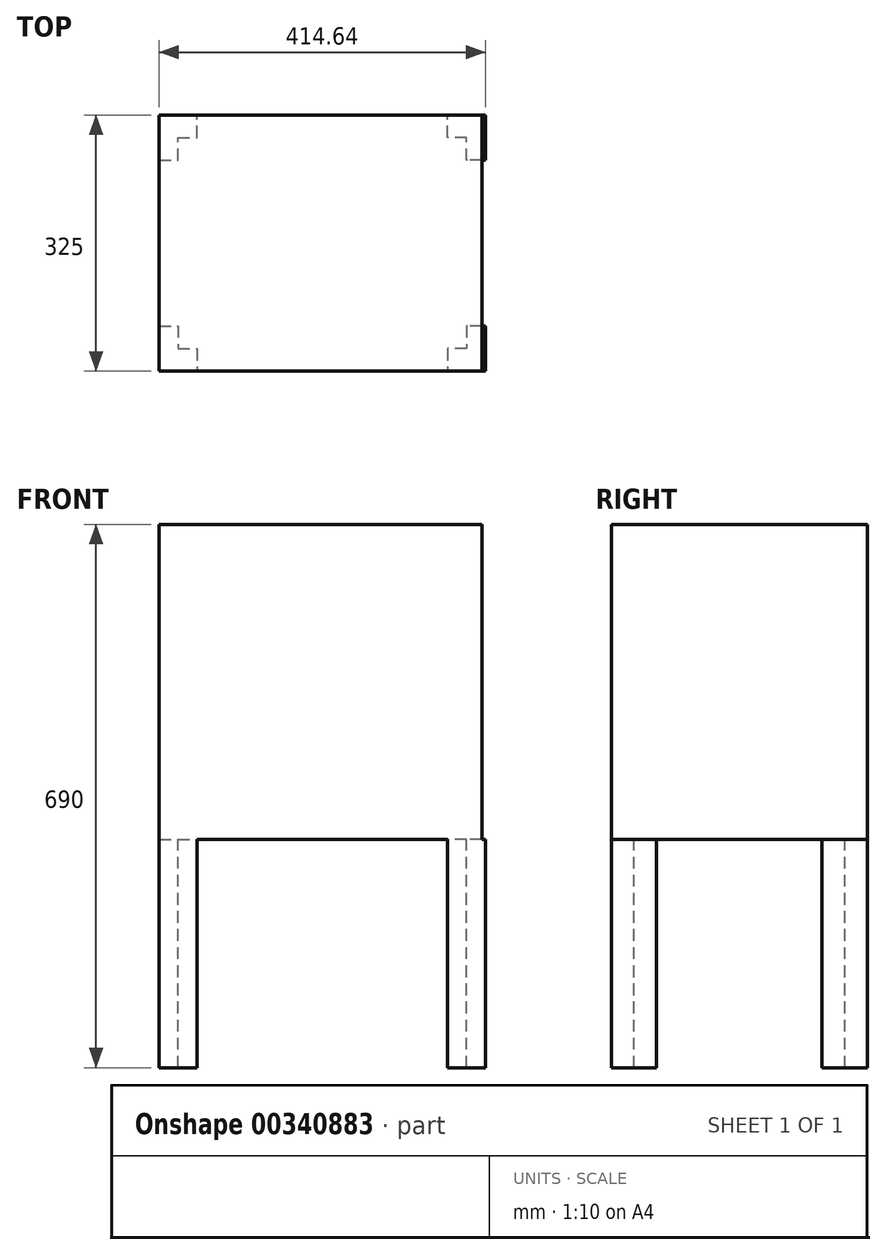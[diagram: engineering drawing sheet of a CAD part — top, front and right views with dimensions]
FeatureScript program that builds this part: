
annotation { "Feature Type Name" : "Feature", "Feature Type Description" : "" }
export const myFeature = defineFeature(function(context is Context, id is Id, definition is map)
    precondition{}
    {
        {
            var Q0;
            Q0=qCreatedBy(makeId("Top.planeOp"),FACE);
            var sketch = newSketch(context, id + "F0", { "sketchPlane" : qUnion([Q0])});
            skLineSegment(sketch, "E0.bottom", {"start": v(-207.32, 208.4) * mm, "end": v(202.68, 208.4) * mm});
            skLineSegment(sketch, "E0.top", {"start": v(-207.32, -116.6) * mm, "end": v(202.68, -116.6) * mm});
            skLineSegment(sketch, "E0.left", {"start": v(-207.32, 208.4) * mm, "end": v(-207.32, -116.6) * mm});
            skLineSegment(sketch, "E0.right", {"start": v(202.68, 208.4) * mm, "end": v(202.68, -116.6) * mm});
            skSolve(sketch);
        }
        {
            var Q0;
            Q0=makeQuery(id+"F0.imprint","IMPRINT",FACE,{"disambiguationData":[TD([[makeQuery(id+"F0.imprint","IMPRINT",EDGE,{"derivedFrom":sQuery(id+"F0.wireOp",EDGE,"E0.bottom")}),-1.0]])]});
            extrude(context, id + "F1", {"entities" : qUnion([Q0]), "depth" : 400 * mm});
        }
        {
            var Q0;
            Q0=makeQuery(id+"F1.opExtrude","CAP_FACE",FACE,{"disambiguationData":[OSD([sQuery(id+"F0.wireOp",EDGE,"E0.bottom"),sQuery(id+"F0.wireOp",EDGE,"E0.top"),sQuery(id+"F0.wireOp",EDGE,"E0.left"),sQuery(id+"F0.wireOp",EDGE,"E0.right")])],"isStart":true});
            var sketch = newSketch(context, id + "F2", { "sketchPlane" : qUnion([Q0])});
            skLineSegment(sketch, "E1", {"start": v(-207.32, 116.6) * mm, "end": v(-207.32, 59.23) * mm});
            skLineSegment(sketch, "E2", {"start": v(-207.32, 59.23) * mm, "end": v(-183.46, 59.23) * mm});
            skLineSegment(sketch, "E3", {"start": v(-183.46, 59.23) * mm, "end": v(-183.46, 88.22) * mm});
            skLineSegment(sketch, "E4", {"start": v(-183.46, 88.22) * mm, "end": v(-159.29, 88.22) * mm});
            skLineSegment(sketch, "E5", {"start": v(-159.29, 88.22) * mm, "end": v(-159.29, 116.6) * mm});
            skLineSegment(sketch, "E6", {"start": v(-159.29, 116.6) * mm, "end": v(-207.32, 116.6) * mm});
            skLineSegment(sketch, "E7", {"start": v(0, -252.73) * mm, "end": v(0, 278.32) * mm, "construction": true});
            skLineSegment(sketch, "E8", {"start": v(-257.09, -45.9) * mm, "end": v(353.38, -45.9) * mm, "construction": true});
            skLineSegment(sketch, "E9.MirrorCS", {"start": v(159.29, 88.22) * mm, "end": v(159.29, 116.6) * mm});
            skLineSegment(sketch, "E10.MirrorCS", {"start": v(159.29, 116.6) * mm, "end": v(207.32, 116.6) * mm});
            skLineSegment(sketch, "E11.MirrorCS", {"start": v(207.32, 116.6) * mm, "end": v(207.32, 59.23) * mm});
            skLineSegment(sketch, "E12.MirrorCS", {"start": v(207.32, 59.23) * mm, "end": v(183.46, 59.23) * mm});
            skLineSegment(sketch, "E13.MirrorCS", {"start": v(183.46, 59.23) * mm, "end": v(183.46, 88.22) * mm});
            skLineSegment(sketch, "E14.MirrorCS", {"start": v(183.46, 88.22) * mm, "end": v(159.29, 88.22) * mm});
            skLineSegment(sketch, "E15.MirrorCS", {"start": v(-207.32, -151.02) * mm, "end": v(-183.46, -151.02) * mm});
            skLineSegment(sketch, "E16.MirrorCS", {"start": v(-207.32, -208.4) * mm, "end": v(-207.32, -151.02) * mm});
            skLineSegment(sketch, "E17.MirrorCS", {"start": v(-159.29, -208.4) * mm, "end": v(-207.32, -208.4) * mm});
            skLineSegment(sketch, "E18.MirrorCS", {"start": v(-159.29, -180) * mm, "end": v(-159.29, -208.4) * mm});
            skLineSegment(sketch, "E19.MirrorCS", {"start": v(-183.46, -180) * mm, "end": v(-159.29, -180) * mm});
            skLineSegment(sketch, "E20.MirrorCS", {"start": v(-183.46, -151.02) * mm, "end": v(-183.46, -180) * mm});
            skLineSegment(sketch, "E21.MirrorCS", {"start": v(159.29, -180) * mm, "end": v(159.29, -208.4) * mm});
            skLineSegment(sketch, "E22.MirrorCS", {"start": v(183.46, -180) * mm, "end": v(159.29, -180) * mm});
            skLineSegment(sketch, "E23.MirrorCS", {"start": v(183.46, -151.02) * mm, "end": v(183.46, -180) * mm});
            skLineSegment(sketch, "E24.MirrorCS", {"start": v(207.32, -151.02) * mm, "end": v(183.46, -151.02) * mm});
            skLineSegment(sketch, "E25.MirrorCS", {"start": v(207.32, -208.4) * mm, "end": v(207.32, -151.02) * mm});
            skLineSegment(sketch, "E26.MirrorCS", {"start": v(159.29, -208.4) * mm, "end": v(207.32, -208.4) * mm});
            skSolve(sketch);
        }
        {
            var Q0;
            Q0=makeQuery(id+"F2.imprint","IMPRINT",FACE,{"disambiguationData":[TD([[makeQuery(id+"F2.imprint","IMPRINT",EDGE,{"derivedFrom":sQuery(id+"F2.wireOp",EDGE,"E15.MirrorCS")}),-1.0]])]});
            var Q1;
            {var subQ3=sQuery(id+"F2.wireOp",EDGE,"E11.MirrorCS");Q1=makeQuery(id+"F2.imprint","IMPRINT",FACE,{"disambiguationData":[TD([[makeQuery(id+"F2.imprint","IMPRINT",EDGE,{"derivedFrom":subQ3}),-1.0]])]});}
            var Q2;
            {var subQ0=sQuery(id+"F2.wireOp",EDGE,"E25.MirrorCS");Q2=makeQuery(id+"F2.imprint","IMPRINT",FACE,{"disambiguationData":[TD([[makeQuery(id+"F2.imprint","IMPRINT",EDGE,{"derivedFrom":subQ0}),1.0]])]});}
            var Q3;
            {var subQ4=sQuery(id+"F2.wireOp",EDGE,"E9.MirrorCS");Q3=makeQuery(id+"F2.imprint","IMPRINT",FACE,{"disambiguationData":[TD([[makeQuery(id+"F2.imprint","IMPRINT",EDGE,{"derivedFrom":subQ4}),-1.0]])]});}
            var Q4;
            {var subQ4=sQuery(id+"F2.wireOp",EDGE,"E21.MirrorCS");Q4=makeQuery(id+"F2.imprint","IMPRINT",FACE,{"disambiguationData":[TD([[makeQuery(id+"F2.imprint","IMPRINT",EDGE,{"derivedFrom":subQ4}),1.0]])]});}
            var Q5;
            Q5=makeQuery(id+"F2.imprint","IMPRINT",FACE,{"disambiguationData":[TD([[makeQuery(id+"F2.imprint","IMPRINT",EDGE,{"derivedFrom":sQuery(id+"F2.wireOp",EDGE,"E1")}),-1.0]])]});
            extrude(context, id + "F3", {"entities" : qUnion([Q0, Q1, Q2, Q3, Q4, Q5]), "operationType" : NewBodyOperationType.ADD, "depth" : 290 * mm});
        }
    });
